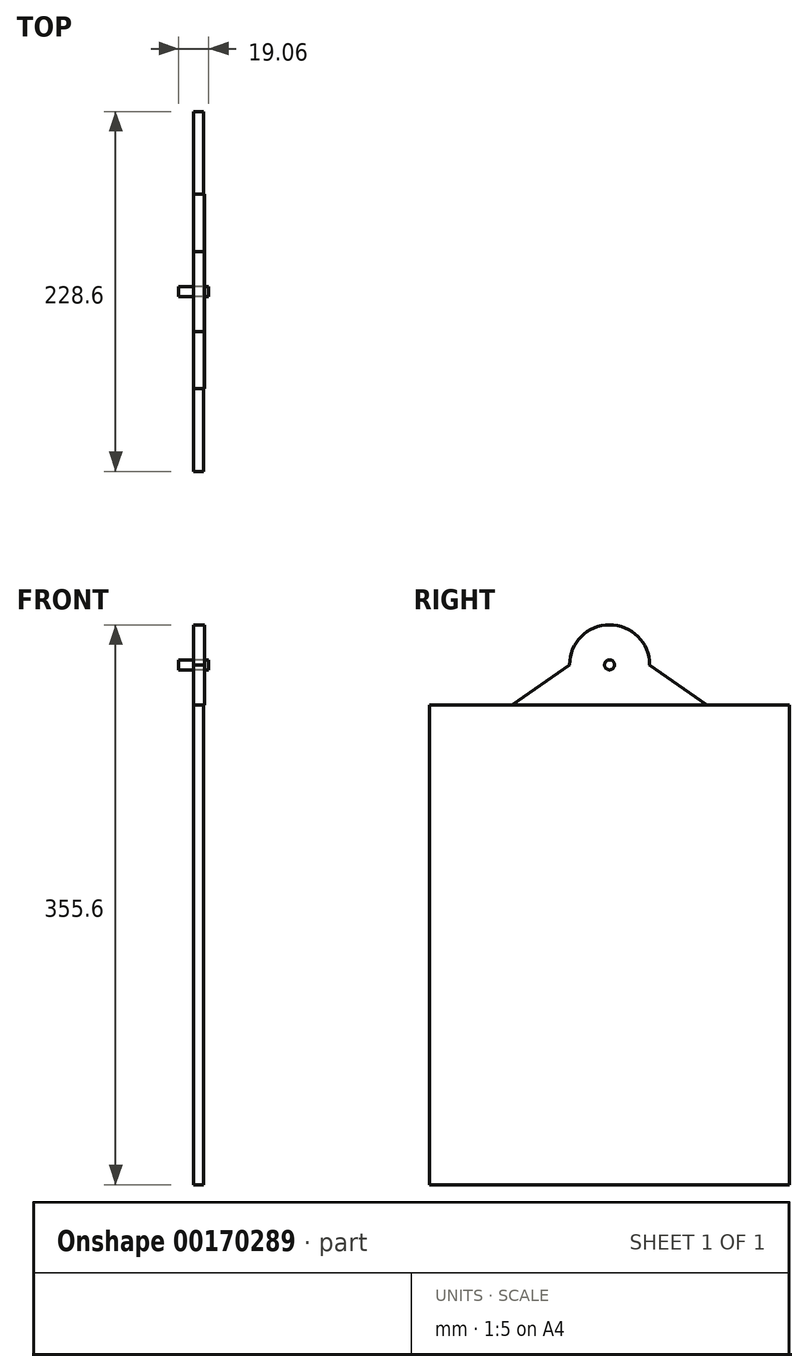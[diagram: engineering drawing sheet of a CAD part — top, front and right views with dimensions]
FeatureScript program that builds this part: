
annotation { "Feature Type Name" : "Feature", "Feature Type Description" : "" }
export const myFeature = defineFeature(function(context is Context, id is Id, definition is map)
    precondition{}
    {
        {
            var Q0;
            Q0=qCreatedBy(makeId("Right.planeOp"),FACE);
            var sketch = newSketch(context, id + "F0", { "sketchPlane" : qUnion([Q0])});
            skCircle(sketch, "E0", {"center": v(0, 0) * mm, "radius": 3.18 * mm});
            skLineSegment(sketch, "E1", {"start": v(0, 0) * mm, "end": v(0, -25.4) * mm});
            skLineSegment(sketch, "E2", {"start": v(0, -25.4) * mm, "end": v(-114.3, -25.4) * mm});
            skLineSegment(sketch, "E3.bottom", {"start": v(-114.3, -25.4) * mm, "end": v(114.3, -25.4) * mm});
            skLineSegment(sketch, "E3.top", {"start": v(-114.3, -330.2) * mm, "end": v(114.3, -330.2) * mm});
            skLineSegment(sketch, "E3.left", {"start": v(-114.3, -25.4) * mm, "end": v(-114.3, -330.2) * mm});
            skLineSegment(sketch, "E3.right", {"start": v(114.3, -25.4) * mm, "end": v(114.3, -330.2) * mm});
            skCircle(sketch, "E4", {"center": v(0, 0) * mm, "radius": 25.4 * mm});
            skLineSegment(sketch, "E5", {"start": v(-25.4, 0) * mm, "end": v(-61.88, -25.4) * mm});
            skLineSegment(sketch, "E6", {"start": v(25.4, 0) * mm, "end": v(61.88, -25.4) * mm});
            skSolve(sketch);
        }
        {
            var Q0;
            Q0=makeQuery(id+"F0.imprint","IMPRINT",FACE,{"disambiguationData":[TD([[makeQuery(id+"F0.imprint","IMPRINT",EDGE,{"derivedFrom":sQuery(id+"F0.wireOp",EDGE,"E0")}),1.0]])]});
            extrude(context, id + "F1", {"entities" : qUnion([Q0]), "endBound" : BoundingType.SYMMETRIC, "depth" : 19.05 * mm});
        }
        {
            var Q0;
            Q0=makeQuery(id+"F0.imprint","IMPRINT",FACE,{"disambiguationData":[TD([[makeQuery(id+"F0.imprint","IMPRINT",EDGE,{"derivedFrom":sQuery(id+"F0.wireOp",EDGE,"E3.top")}),1.0]])]});
            extrude(context, id + "F2", {"entities" : qUnion([Q0]), "depth" : 6.35 * mm});
        }
        {
            var Q0;
            {var subQ3=sQuery(id+"F0.wireOp",EDGE,"E5");Q0=makeQuery(id+"F0.imprint","IMPRINT",FACE,{"disambiguationData":[TD([[makeQuery(id+"F0.imprint","IMPRINT",EDGE,{"derivedFrom":subQ3}),1.0]])]});}
            var Q1;
            Q1=makeQuery(id+"F0.imprint","IMPRINT",FACE,{"disambiguationData":[TD([[makeQuery(id+"F0.imprint","IMPRINT",EDGE,{"derivedFrom":sQuery(id+"F0.wireOp",EDGE,"E0")}),-1.0]])]});
            var Q2;
            {var subQ3=sQuery(id+"F0.wireOp",EDGE,"E6");Q2=makeQuery(id+"F0.imprint","IMPRINT",FACE,{"disambiguationData":[TD([[makeQuery(id+"F0.imprint","IMPRINT",EDGE,{"derivedFrom":subQ3}),-1.0]])]});}
            extrude(context, id + "F3", {"entities" : qUnion([Q0, Q1, Q2]), "depth" : 6.86 * mm});
        }
    });
